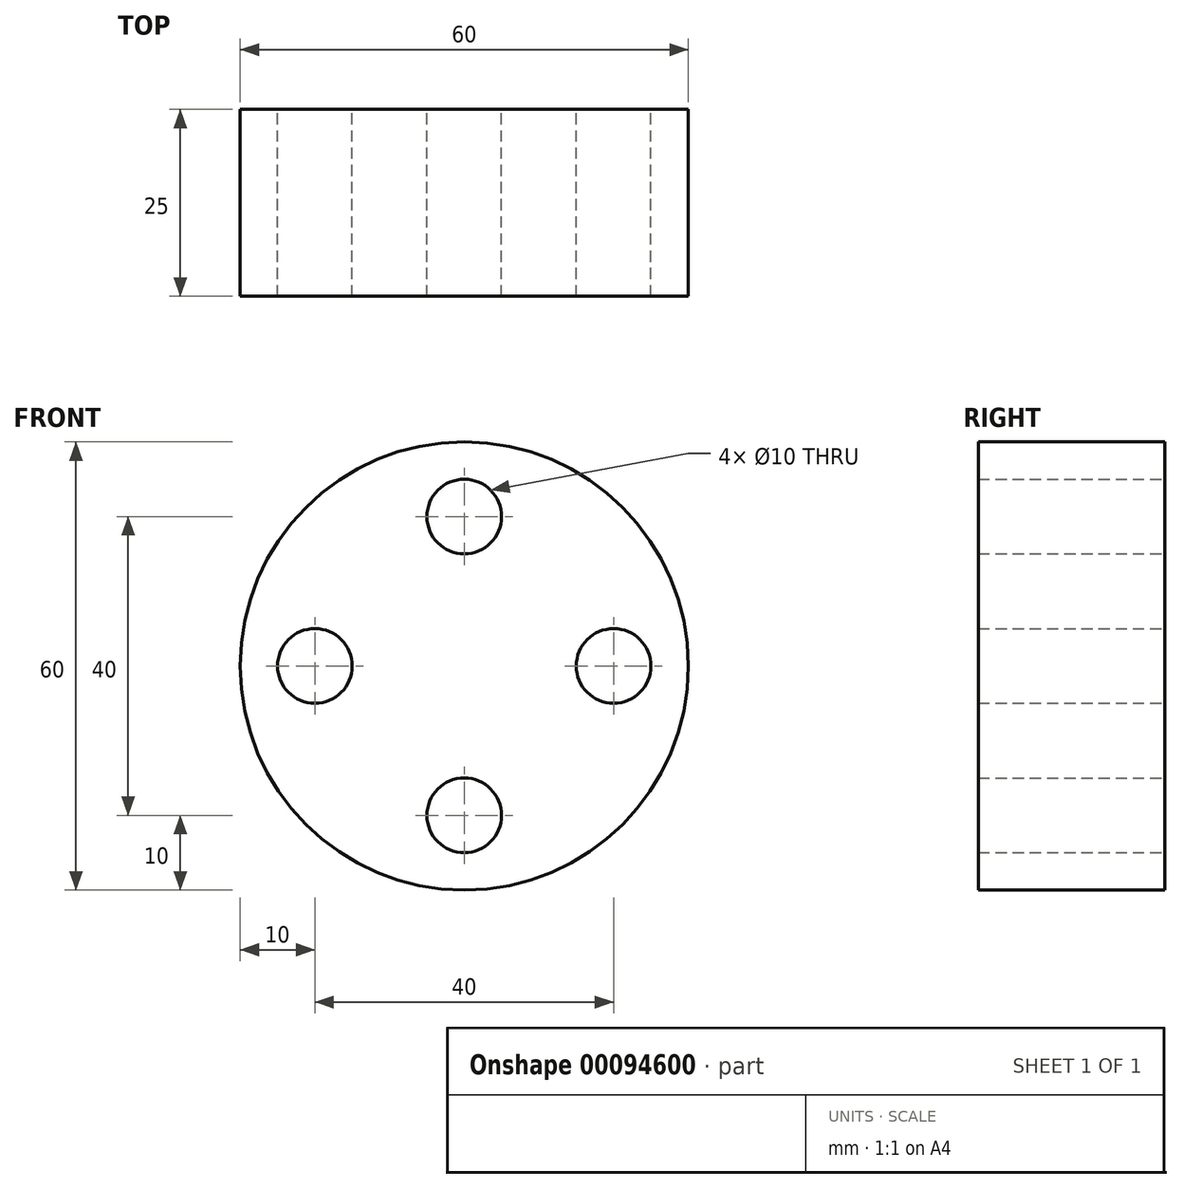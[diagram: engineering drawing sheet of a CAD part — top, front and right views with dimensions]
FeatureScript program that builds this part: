
annotation { "Feature Type Name" : "Feature", "Feature Type Description" : "" }
export const myFeature = defineFeature(function(context is Context, id is Id, definition is map)
    precondition{}
    {
        {
            var Q0;
            Q0=qCreatedBy(makeId("Front.planeOp"),FACE);
            var sketch = newSketch(context, id + "F0", { "sketchPlane" : qUnion([Q0])});
            skCircle(sketch, "E0", {"center": v(0, 0) * mm, "radius": 30 * mm});
            skCircle(sketch, "E1", {"center": v(0, 0) * mm, "radius": 20 * mm, "construction": true});
            skLineSegment(sketch, "E2", {"start": v(-30, 0) * mm, "end": v(30, 0) * mm});
            skLineSegment(sketch, "E3", {"start": v(0, 0) * mm, "end": v(0, 30) * mm});
            skLineSegment(sketch, "E4", {"start": v(0, 30) * mm, "end": v(0, -30) * mm});
            skCircle(sketch, "E5", {"center": v(-20, 0) * mm, "radius": 5 * mm});
            skCircle(sketch, "E6.1.0", {"center": v(0, -20) * mm, "radius": 5 * mm});
            skCircle(sketch, "E6.2.0", {"center": v(20, 0) * mm, "radius": 5 * mm});
            skCircle(sketch, "E6.3.0", {"center": v(0, 20) * mm, "radius": 5 * mm});
            skLineSegment(sketch, "E6.anchor1", {"start": v(0, 0) * mm, "end": v(-20, 0) * mm, "construction": true});
            skLineSegment(sketch, "E6.anchor2", {"start": v(0, 0) * mm, "end": v(0, 20) * mm, "construction": true});
            skSolve(sketch);
        }
        {
            var Q0;
            {var subQ1=sQuery(id+"F0.wireOp",EDGE,"E0");var subQ5=sQuery(id+"F0.wireOp",EDGE,"E2");var subQ6=makeQuery(id+"F0.imprint","INTERSECT",VERTEX,{"disambiguationData":[OD(1.0)],"derivedFrom":[subQ1,subQ5]});Q0=makeQuery(id+"F0.imprint","IMPRINT",FACE,{"disambiguationData":[TD([[makeQuery(id+"F0.imprint","IMPRINT",EDGE,{"disambiguationData":[TD([[subQ6,-1.0]])],"derivedFrom":subQ1}),1.0]])]});}
            var Q1;
            {var subQ1=sQuery(id+"F0.wireOp",EDGE,"E0");var subQ6=sQuery(id+"F0.wireOp",EDGE,"E2");var subQ9=makeQuery(id+"F0.imprint","INTERSECT",VERTEX,{"disambiguationData":[OD(0.0)],"derivedFrom":[subQ1,subQ6]});Q1=makeQuery(id+"F0.imprint","IMPRINT",FACE,{"disambiguationData":[TD([[makeQuery(id+"F0.imprint","IMPRINT",EDGE,{"disambiguationData":[TD([[subQ9,1.0]])],"derivedFrom":subQ1}),1.0]])]});}
            var Q2;
            {var subQ1=sQuery(id+"F0.wireOp",EDGE,"E2");var subQ8=sQuery(id+"F0.wireOp",EDGE,"E0");var subQ9=makeQuery(id+"F0.imprint","INTERSECT",VERTEX,{"disambiguationData":[OD(0.0)],"derivedFrom":[subQ8,subQ1]});Q2=makeQuery(id+"F0.imprint","IMPRINT",FACE,{"disambiguationData":[TD([[makeQuery(id+"F0.imprint","IMPRINT",EDGE,{"disambiguationData":[TD([[subQ9,-1.0]])],"derivedFrom":subQ8}),1.0]])]});}
            var Q3;
            {var subQ1=sQuery(id+"F0.wireOp",EDGE,"E2");var subQ5=sQuery(id+"F0.wireOp",EDGE,"E0");var subQ6=makeQuery(id+"F0.imprint","INTERSECT",VERTEX,{"disambiguationData":[OD(1.0)],"derivedFrom":[subQ5,subQ1]});Q3=makeQuery(id+"F0.imprint","IMPRINT",FACE,{"disambiguationData":[TD([[makeQuery(id+"F0.imprint","IMPRINT",EDGE,{"disambiguationData":[TD([[subQ6,1.0]])],"derivedFrom":subQ5}),1.0]])]});}
            extrude(context, id + "F1", {"entities" : qUnion([Q0, Q1, Q2, Q3]), "depth" : 25 * mm});
        }
    });
